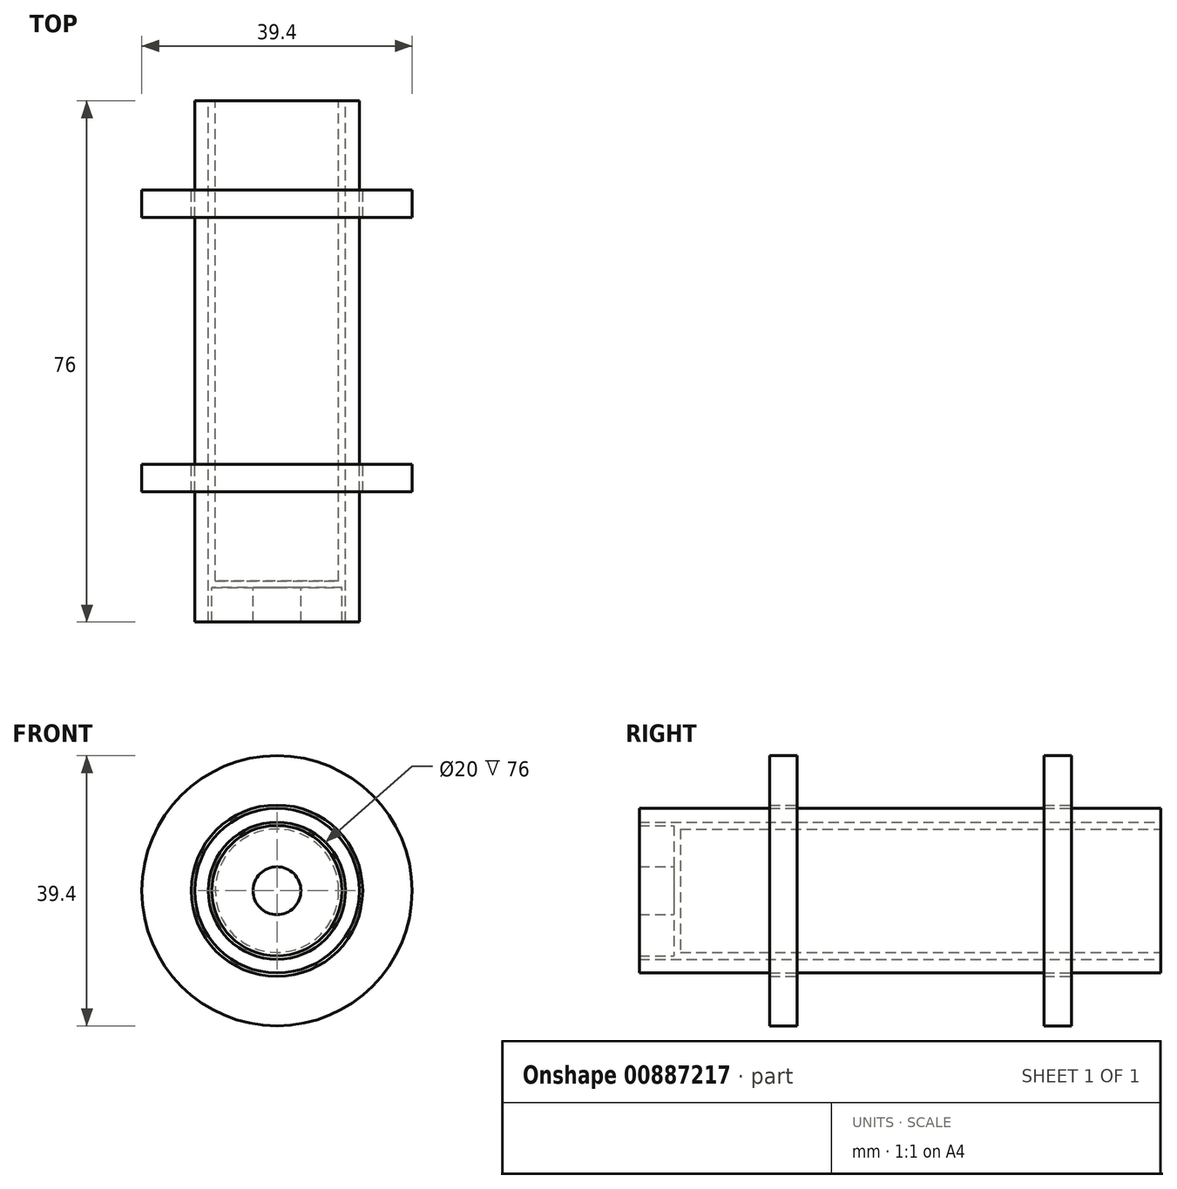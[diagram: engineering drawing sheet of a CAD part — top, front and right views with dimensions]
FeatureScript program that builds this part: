
annotation { "Feature Type Name" : "Feature", "Feature Type Description" : "" }
export const myFeature = defineFeature(function(context is Context, id is Id, definition is map)
    precondition{}
    {
        {
            var Q0;
            Q0=qCreatedBy(makeId("Right.planeOp"),FACE);
            var sketch = newSketch(context, id + "F0", { "sketchPlane" : qUnion([Q0])});
            skLineSegment(sketch, "E0.bottom", {"start": v(35, 0) * mm, "end": v(-35, 0) * mm});
            skLineSegment(sketch, "E0.top", {"start": v(35, -9) * mm, "end": v(-35, -9) * mm});
            skLineSegment(sketch, "E0.left", {"start": v(35, 0) * mm, "end": v(35, -9) * mm});
            skLineSegment(sketch, "E0.right", {"start": v(-35, 0) * mm, "end": v(-35, -9) * mm});
            skPoint(sketch, "E0.middle", {"position": v(0, -4.5) * mm});
            skSolve(sketch);
        }
        {
            var Q0;
            Q0=makeQuery(id+"F0.imprint","IMPRINT",FACE,{"disambiguationData":[TD([[makeQuery(id+"F0.imprint","IMPRINT",EDGE,{"derivedFrom":sQuery(id+"F0.wireOp",EDGE,"E0.bottom")}),1.0]])]});
            var Q1;
            Q1=sQuery(id+"F0.wireOp",EDGE,"E0.bottom");
            revolve(context, id + "F1", {"entities" : qUnion([Q0]), "axis" : qUnion([Q1]), "revolveType" : RevolveType.FULL});
        }
        {
            var Q0;
            Q0=qCreatedBy(makeId("Right.planeOp"),FACE);
            var sketch = newSketch(context, id + "F2", { "sketchPlane" : qUnion([Q0])});
            skLineSegment(sketch, "E1.bottom", {"start": v(35, -10) * mm, "end": v(-41, -10) * mm});
            skLineSegment(sketch, "E1.top", {"start": v(35, -12) * mm, "end": v(-41, -12) * mm});
            skLineSegment(sketch, "E1.left", {"start": v(35, -10) * mm, "end": v(35, -12) * mm});
            skLineSegment(sketch, "E1.right", {"start": v(-41, -10) * mm, "end": v(-41, -12) * mm});
            skPoint(sketch, "E1.middle", {"position": v(-3, -11) * mm});
            skLineSegment(sketch, "E2", {"start": v(51.51, 0) * mm, "end": v(-46.56, 0) * mm});
            skSolve(sketch);
        }
        {
            var Q0;
            Q0=qSketchRegion(id+"F2",true);
            var Q1;
            Q1=sQuery(id+"F2.wireOp",EDGE,"E2");
            revolve(context, id + "F3", {"surfaceOperationType" : NewSurfaceOperationType.NEW, "entities" : qUnion([Q0]), "axis" : qUnion([Q1]), "revolveType" : RevolveType.FULL});
        }
        {
            var Q0;
            Q0=qCreatedBy(makeId("Right.planeOp"),FACE);
            var sketch = newSketch(context, id + "F4", { "sketchPlane" : qUnion([Q0])});
            skLineSegment(sketch, "E3.bottom", {"start": v(-22, -12.5) * mm, "end": v(-18, -12.5) * mm});
            skLineSegment(sketch, "E3.top", {"start": v(-22, -19.7) * mm, "end": v(-18, -19.7) * mm});
            skLineSegment(sketch, "E3.left", {"start": v(-22, -12.5) * mm, "end": v(-22, -19.7) * mm});
            skLineSegment(sketch, "E3.right", {"start": v(22, -12.5) * mm, "end": v(22, -19.7) * mm});
            skPoint(sketch, "E3.middle", {"position": v(0, -16.1) * mm});
            skLineSegment(sketch, "E4.left", {"start": v(-18, -12.5) * mm, "end": v(-18, -19.7) * mm});
            skLineSegment(sketch, "E4.right", {"start": v(18, -12.5) * mm, "end": v(18, -19.7) * mm});
            skLineSegment(sketch, "E5.trimOffspring", {"start": v(18, -19.7) * mm, "end": v(22, -19.7) * mm});
            skLineSegment(sketch, "E6.trimOffspring", {"start": v(18, -12.5) * mm, "end": v(22, -12.5) * mm});
            skSolve(sketch);
        }
        {
            var Q0;
            Q0=qSketchRegion(id+"F4",true);
            var Q1;
            Q1=sQuery(id+"F2.wireOp",EDGE,"E2");
            revolve(context, id + "F5", {"surfaceOperationType" : NewSurfaceOperationType.NEW, "entities" : qUnion([Q0]), "axis" : qUnion([Q1]), "revolveType" : RevolveType.FULL});
        }
        {
            var Q0;
            Q0=qCreatedBy(makeId("Right.planeOp"),FACE);
            var sketch = newSketch(context, id + "F6", { "sketchPlane" : qUnion([Q0])});
            skLineSegment(sketch, "E7.bottom", {"start": v(-36, -3.5) * mm, "end": v(-41, -3.5) * mm});
            skLineSegment(sketch, "E7.top", {"start": v(-36, -9.5) * mm, "end": v(-41, -9.5) * mm});
            skLineSegment(sketch, "E7.left", {"start": v(-36, -3.5) * mm, "end": v(-36, -9.5) * mm});
            skLineSegment(sketch, "E7.right", {"start": v(-41, -3.5) * mm, "end": v(-41, -9.5) * mm});
            skPoint(sketch, "E7.middle", {"position": v(-38.5, -6.5) * mm});
            skSolve(sketch);
        }
        {
            var Q0;
            Q0=qSketchRegion(id+"F6",true);
            var Q1;
            Q1=sQuery(id+"F2.wireOp",EDGE,"E2");
            revolve(context, id + "F7", {"surfaceOperationType" : NewSurfaceOperationType.NEW, "entities" : qUnion([Q0]), "axis" : qUnion([Q1]), "revolveType" : RevolveType.FULL});
        }
    });
